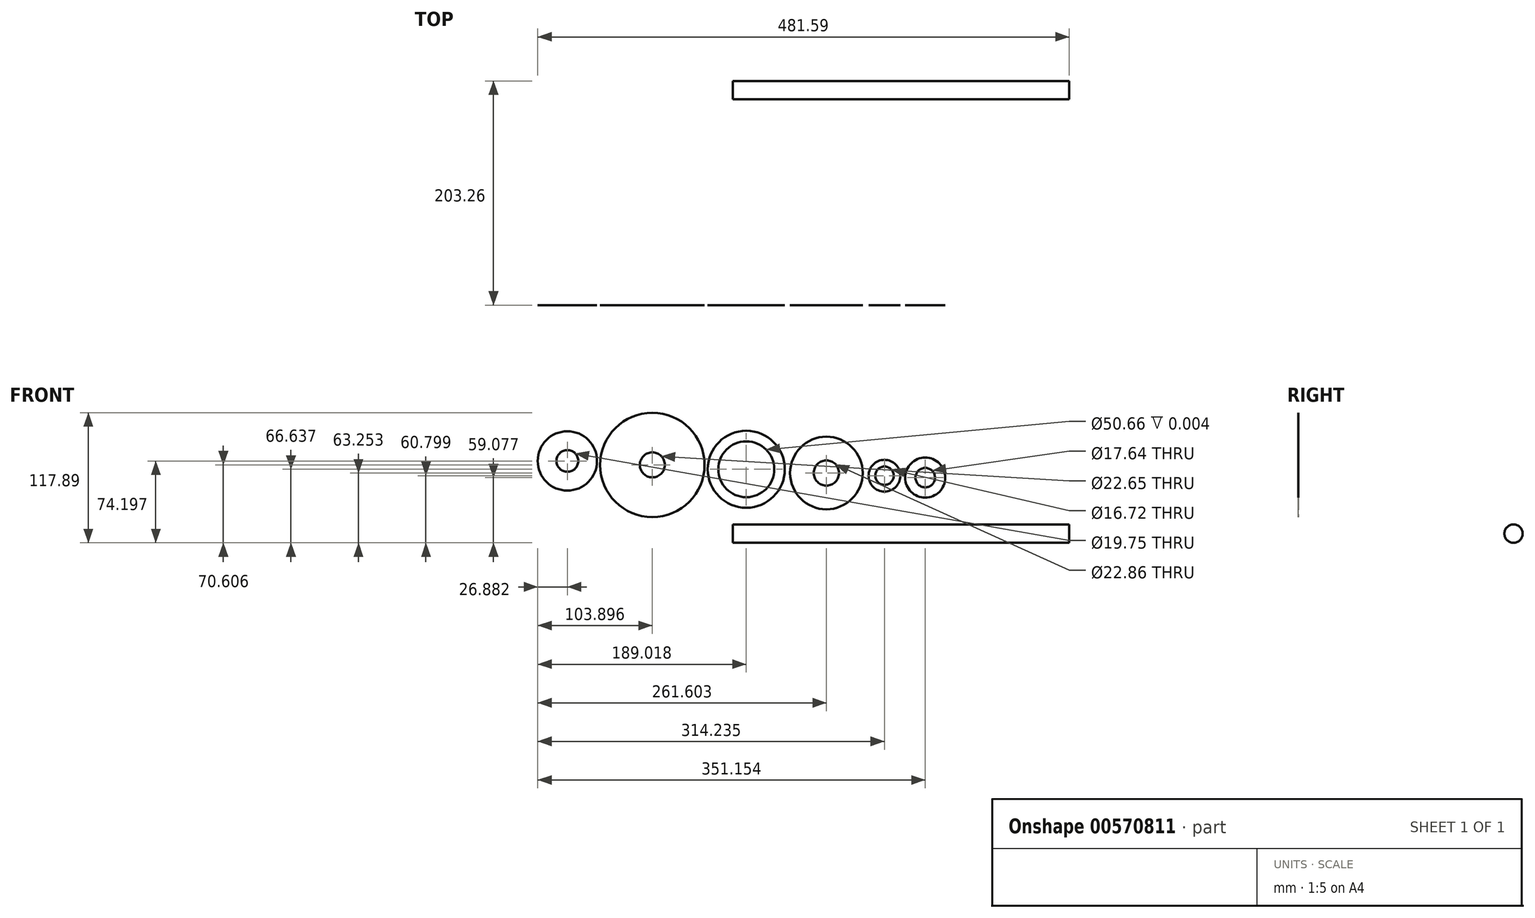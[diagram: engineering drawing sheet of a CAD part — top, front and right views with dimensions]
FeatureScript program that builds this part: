
annotation { "Feature Type Name" : "Feature", "Feature Type Description" : "" }
export const myFeature = defineFeature(function(context is Context, id is Id, definition is map)
    precondition{}
    {
        {
            var Q0;
            Q0=qCreatedBy(makeId("Front.planeOp"),FACE);
            var sketch = newSketch(context, id + "F0", { "sketchPlane" : qUnion([Q0])});
            skLineSegment(sketch, "E0", {"start": v(-149.9, 65.89) * mm, "end": v(174.36, 50.77) * mm, "construction": true});
            skPoint(sketch, "E1", {"position": v(137.45, 52.49) * mm});
            skPoint(sketch, "E2", {"position": v(84.81, 54.94) * mm});
            skPoint(sketch, "E3", {"position": v(12.23, 58.33) * mm});
            skPoint(sketch, "E4", {"position": v(-72.9, 62.3) * mm});
            skCircle(sketch, "E5", {"center": v(174.36, 50.77) * mm, "radius": 12.53 * mm, "construction": true});
            skCircle(sketch, "E6", {"center": v(174.36, 50.77) * mm, "radius": 8.82 * mm});
            skCircle(sketch, "E7", {"center": v(174.36, 50.77) * mm, "radius": 18.17 * mm});
            skCircle(sketch, "E8", {"center": v(137.45, 52.49) * mm, "radius": 14.4 * mm});
            skCircle(sketch, "E9", {"center": v(137.45, 52.49) * mm, "radius": 8.36 * mm});
            skCircle(sketch, "E10", {"center": v(84.81, 54.94) * mm, "radius": 32.91 * mm});
            skCircle(sketch, "E11", {"center": v(84.81, 54.94) * mm, "radius": 11.43 * mm});
            skCircle(sketch, "E12", {"center": v(12.23, 58.33) * mm, "radius": 34.92 * mm});
            skCircle(sketch, "E13", {"center": v(12.23, 58.33) * mm, "radius": 25.33 * mm});
            skCircle(sketch, "E14", {"center": v(-72.9, 62.3) * mm, "radius": 47.28 * mm});
            skCircle(sketch, "E15", {"center": v(-72.9, 62.3) * mm, "radius": 11.32 * mm});
            skCircle(sketch, "E16", {"center": v(-149.9, 65.89) * mm, "radius": 26.88 * mm});
            skCircle(sketch, "E17", {"center": v(-149.9, 65.89) * mm, "radius": 9.88 * mm});
            skSolve(sketch);
        }
        {
            var Q0;
            Q0 = qSketchRegion(id + "F0", true);
            extrude(context, id + "F1", {"entities" : qUnion([Q0]), "depth" : 3 / 812.8 * mm, "offsetDistance" : 25.4 * mm});
        }
        {
            var Q0;
            Q0=qCreatedBy(makeId("Right.planeOp"),FACE);
            var sketch = newSketch(context, id + "F2", { "sketchPlane" : qUnion([Q0])});
            skCircle(sketch, "E18", {"center": v(194.95, 0) * mm, "radius": 8.3 * mm});
            skSolve(sketch);
        }
        {
            var Q0;
            Q0 = qSketchRegion(id + "F2", true);
            extrude(context, id + "F3", {"entities" : qUnion([Q0]), "depth" : 304.8 * mm, "offsetDistance" : 25.4 * mm});
        }
    });
